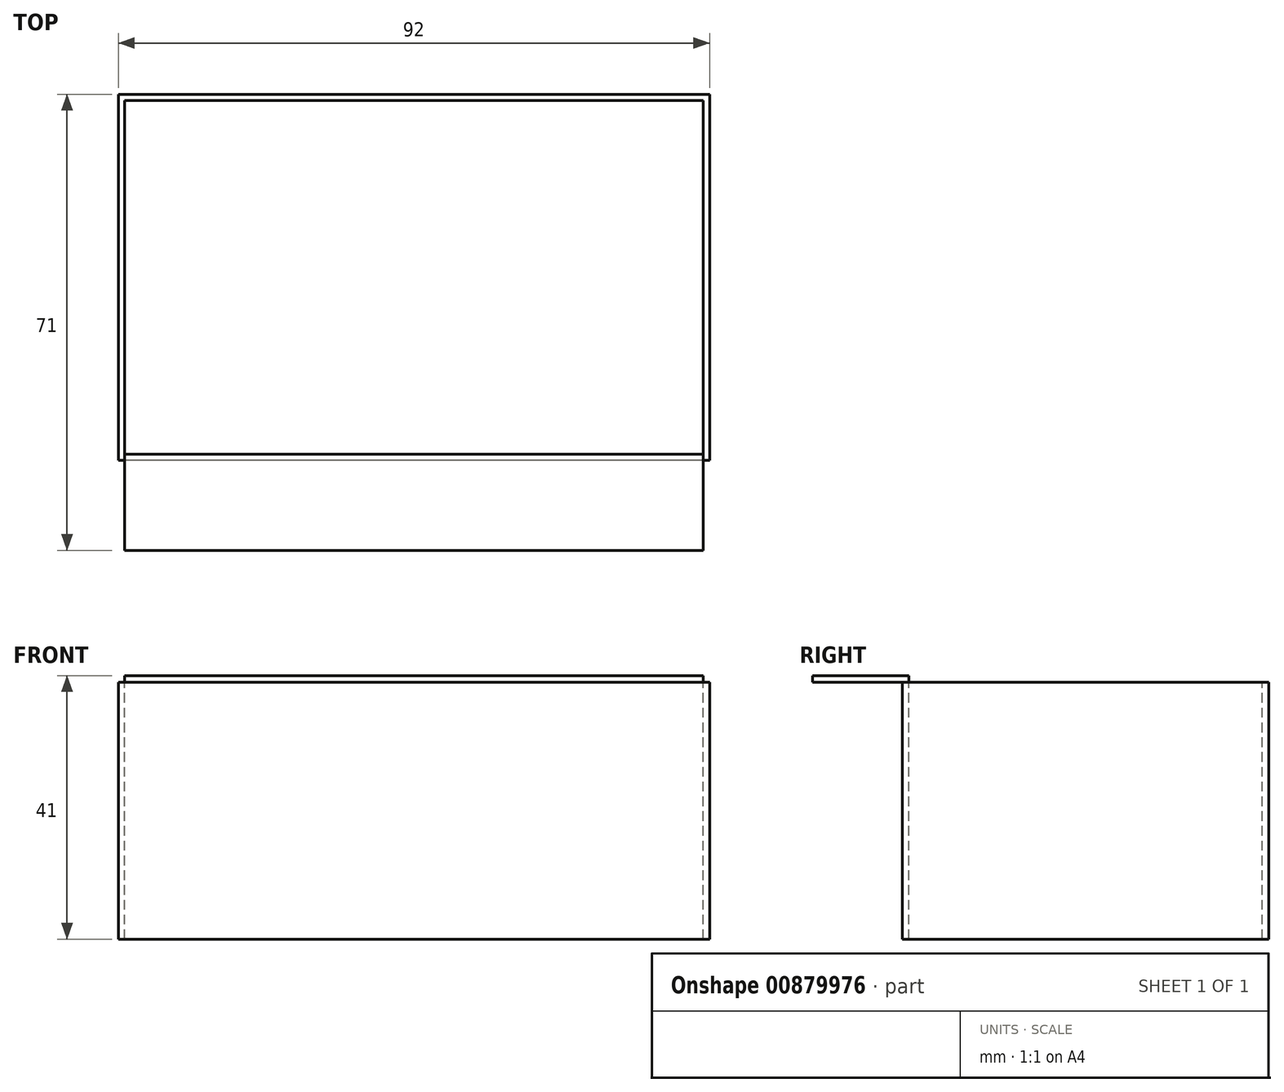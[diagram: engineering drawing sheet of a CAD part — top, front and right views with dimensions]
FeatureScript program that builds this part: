
annotation { "Feature Type Name" : "Feature", "Feature Type Description" : "" }
export const myFeature = defineFeature(function(context is Context, id is Id, definition is map)
    precondition{}
    {
        {
            var Q0;
            Q0=qCreatedBy(makeId("Top.planeOp"),FACE);
            var sketch = newSketch(context, id + "F0", { "sketchPlane" : qUnion([Q0])});
            skLineSegment(sketch, "E0.bottom", {"start": v(-45, 27.5) * mm, "end": v(45, 27.5) * mm});
            skLineSegment(sketch, "E0.top", {"start": v(-45, -27.5) * mm, "end": v(45, -27.5) * mm});
            skLineSegment(sketch, "E0.left", {"start": v(-45, 27.5) * mm, "end": v(-45, -27.5) * mm});
            skLineSegment(sketch, "E0.right", {"start": v(45, 27.5) * mm, "end": v(45, -27.5) * mm});
            skPoint(sketch, "E0.middle", {"position": v(0, 0) * mm});
            skLineSegment(sketch, "E1.bottom", {"start": v(46, 28.5) * mm, "end": v(-46, 28.5) * mm});
            skLineSegment(sketch, "E1.top", {"start": v(46, -28.5) * mm, "end": v(-46, -28.5) * mm});
            skLineSegment(sketch, "E1.left", {"start": v(46, 28.5) * mm, "end": v(46, -28.5) * mm});
            skLineSegment(sketch, "E1.right", {"start": v(-46, 28.5) * mm, "end": v(-46, -28.5) * mm});
            skSolve(sketch);
        }
        {
            var Q0;
            Q0 = qSketchRegion(id + "F0", true);
            extrude(context, id + "F1", {"entities" : qUnion([Q0]), "oppositeDirection" : true, "depth" : 40 * mm, "offsetDistance" : 25 * mm});
        }
        {
            var Q0;
            Q0=makeQuery(id+"F1.opExtrude","CAP_FACE",FACE,{"disambiguationData":[OSD([sQuery(id+"F0.wireOp",EDGE,"E0.bottom"),sQuery(id+"F0.wireOp",EDGE,"E0.top"),sQuery(id+"F0.wireOp",EDGE,"E0.left"),sQuery(id+"F0.wireOp",EDGE,"E0.right"),sQuery(id+"F0.wireOp",EDGE,"E1.bottom"),sQuery(id+"F0.wireOp",EDGE,"E1.top"),sQuery(id+"F0.wireOp",EDGE,"E1.left"),sQuery(id+"F0.wireOp",EDGE,"E1.right")])],"isStart":true});
            var sketch = newSketch(context, id + "F2", { "sketchPlane" : qUnion([Q0])});
            skLineSegment(sketch, "E2.bottom", {"start": v(45, -27.5) * mm, "end": v(-45, -27.5) * mm});
            skLineSegment(sketch, "E2.top", {"start": v(45, -42.5) * mm, "end": v(-45, -42.5) * mm});
            skLineSegment(sketch, "E2.left", {"start": v(45, -27.5) * mm, "end": v(45, -42.5) * mm});
            skLineSegment(sketch, "E2.right", {"start": v(-45, -27.5) * mm, "end": v(-45, -42.5) * mm});
            skSolve(sketch);
        }
        {
            var Q0;
            Q0 = qSketchRegion(id + "F2", true);
            extrude(context, id + "F3", {"entities" : qUnion([Q0]), "operationType" : NewBodyOperationType.ADD, "depth" : 1 * mm, "offsetDistance" : 25 * mm});
        }
    });
